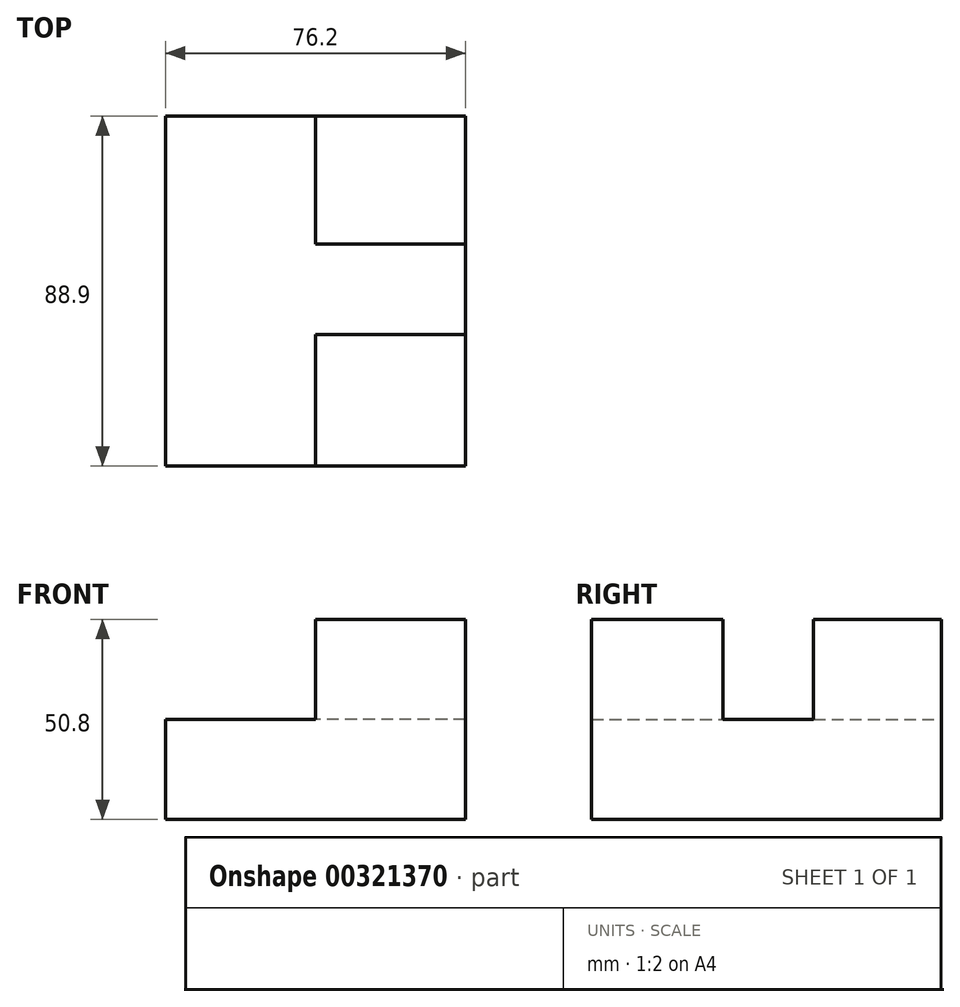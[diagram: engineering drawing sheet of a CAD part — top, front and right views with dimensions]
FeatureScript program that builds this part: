
annotation { "Feature Type Name" : "Feature", "Feature Type Description" : "" }
export const myFeature = defineFeature(function(context is Context, id is Id, definition is map)
    precondition{}
    {
        {
            var Q0;
            Q0=qCreatedBy(makeId("Front.planeOp"),FACE);
            var sketch = newSketch(context, id + "F0", { "sketchPlane" : qUnion([Q0])});
            skLineSegment(sketch, "E0", {"start": v(-69.78, -64.86) * mm, "end": v(6.42, -64.86) * mm});
            skLineSegment(sketch, "E1", {"start": v(6.42, -64.86) * mm, "end": v(6.42, -14.06) * mm});
            skLineSegment(sketch, "E2", {"start": v(6.42, -14.06) * mm, "end": v(-31.68, -14.06) * mm});
            skLineSegment(sketch, "E3", {"start": v(-31.68, -14.06) * mm, "end": v(-31.68, -39.46) * mm});
            skLineSegment(sketch, "E4", {"start": v(-31.68, -39.46) * mm, "end": v(-69.78, -39.46) * mm});
            skLineSegment(sketch, "E5", {"start": v(-69.78, -39.46) * mm, "end": v(-69.78, -64.86) * mm});
            skSolve(sketch);
        }
        {
            var Q0;
            Q0 = qSketchRegion(id + "F0", true);
            extrude(context, id + "F1", {"entities" : qUnion([Q0]), "depth" : 88.9 * mm});
        }
        {
            var Q0;
            Q0=makeQuery(id+"F1.opExtrude","SWEPT_FACE",FACE,{"disambiguationData":[OSD([sQuery(id+"F0.wireOp",EDGE,"E3")])]});
            var sketch = newSketch(context, id + "F2", { "sketchPlane" : qUnion([Q0])});
            skLineSegment(sketch, "E6.bottom", {"start": v(32.45, -14.06) * mm, "end": v(55.52, -14.06) * mm});
            skLineSegment(sketch, "E6.top", {"start": v(32.45, -39.46) * mm, "end": v(55.52, -39.46) * mm});
            skLineSegment(sketch, "E6.left", {"start": v(32.45, -14.06) * mm, "end": v(32.45, -39.46) * mm});
            skLineSegment(sketch, "E6.right", {"start": v(55.52, -14.06) * mm, "end": v(55.52, -39.46) * mm});
            skSolve(sketch);
        }
        {
            var Q0;
            Q0=makeQuery(id+"F2.imprint","IMPRINT",FACE,{"disambiguationData":[TD([[makeQuery(id+"F2.imprint","IMPRINT",EDGE,{"derivedFrom":sQuery(id+"F2.wireOp",EDGE,"E6.bottom")}),1.0]])]});
            var Q1;
            Q1=makeQuery(id+"F2.imprint","IMPRINT",FACE,{"disambiguationData":[TD([[makeQuery(id+"F2.imprint","IMPRINT",EDGE,{"derivedFrom":sQuery(id+"F2.wireOp",EDGE,"E6.top")}),-1.0]])]});
            extrude(context, id + "F3", {"entities" : qUnion([Q0, Q1]), "operationType" : NewBodyOperationType.REMOVE, "endBound" : BoundingType.THROUGH_ALL, "oppositeDirection" : true, "depth" : 25.4 * mm});
        }
    });
